# Revit family: Hager-Orion-IP65-D300-Cl.I-Steel_encl-630A-NoHosted-ES-es
name_source: partatom
category: Electrical Equipment
units: mm (PartAtom-declared; Revit-internal decimal feet)

## family parameters
Always vertical = Yes
Cut with Voids When Loaded = No
Panel Configuration = Two Columns, Circuits Across
Part Type = Panelboard
Room Calculation Point = No
Round Connector Dimension = Use Diameter
Shared = No
Work Plane-Based = Yes

## types (3) — shared parameters
Default Elevation = 1219 mm
EF000003 - Tipo de montaje = EV000384 - Montado superficial (escayola)
EF000007 - Color = EV000270 - Gris
EF000116 - Número RAL = 7035
EF000118 - Con placa de montaje = Yes
EF000339 - Tipo de cubierta = EV004216 - Puerta
EF000437 - Número de entradas de conductos de cables = 2
EF001596 - Material de la carcasa = EV000179 - Acero
EF003532 - Adecuado para uso en exteriores = No
EF004293 - Resistencia al impacto (IK) = EV008784 - IK10
EF004464 - Tipo de puerta = EV002646 - Único
EF005474 - Grado de protección (IP) = EV006421 - IP65
EF006244 - Tapa/puerta transparente = No
EF006306 - Con cierre = Yes
EF007800 - Adecuado para la protección contra rayos = No
EF008873 - Corriente nominal (In) = 630 A
EF009171 - Espesor puerta/tapa = 2 mm  [stored 0.00656168 ft]
EF009554 - Número de aberturas para placas-brida = 2
EF015940 - Tapa con alivio de sobrepresión = No
HG000002 - Con puerta o tapa = Yes
HG000003 - Gama = Orion
HG000006 - Empotrado = No
HG000009 - Puerta batiente doble = No
HG000010 - Puertas asimétricas = No
HG000023 - Caja de doble sección = No
HG000024 - Altura de la sección inferior = 600 mm
HG000026 - Instalación en suelo = No
Manufacturer = Hager
Type Comments = Orion
zero-valued in all types: EF000218 - Profundidad de instalación, EF002950 - Anchura de unidades de división, EF004427 - Número de módulos, HG000027 - Altura de zócalo

## per-type parameters (varying)
| type | EF000008 - Anchura | EF000040 - Altura | EF000049 - Profundidad | EF000266 - Número de filas | EF001088 - Posibilidad de extensión | EF001131 - Profundidad interna | EF001613 - Integridad del circuito | EF009170 - Espesor del material de la caja | EF009212 - Versión de la cubierta | HG000004 - Referencia del fabricante |
| Montado superficial (escayola) IP65 A600 A800 P300  - FL729L | 600 mm | 800 mm  [stored 2.62467 ft] | 300 mm | 1 | Yes | 200 mm  [stored 0.656168 ft] | EV000494 - Ninguno | 1 mm  [stored 0.00328084 ft] | EV000116 - Cerrado | FL729L |
| Montado superficial (escayola) IP65 A800 A1250 P300  - FL730L | 800 mm  [stored 2.62467 ft] | 1250 mm  [stored 4.10105 ft] | 300 mm | 1 | No | 300 mm |  | 2 mm  [stored 0.00656168 ft] | EV009916 - Con muesca | FL730L |
| Montado superficial (escayola) IP65 A800 A1250 P400  - FL731L | 800 mm  [stored 2.62467 ft] | 1250 mm  [stored 4.10105 ft] | 400 mm  [stored 1.31234 ft] | 0 | No | 400 mm  [stored 1.31234 ft] |  | 2 mm  [stored 0.00656168 ft] | EV009916 - Con muesca | FL731L |

note: [stored X ft] marks values corroborated as IEEE doubles in the binary element streams (Revit-internal decimal feet)

## geometry (parser evidence)
native form markers: Blend x4, Sweep x10
no freeform markers — native parametric forms only
